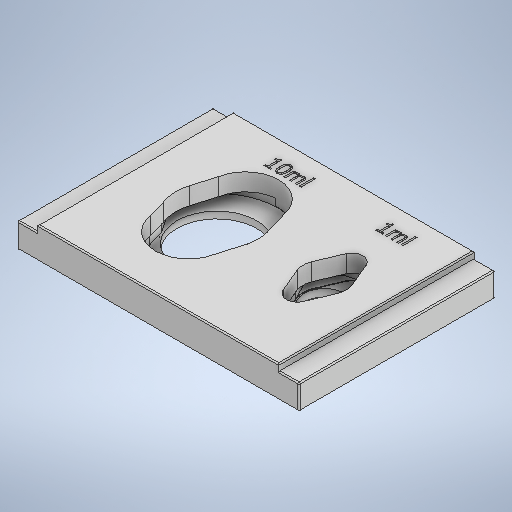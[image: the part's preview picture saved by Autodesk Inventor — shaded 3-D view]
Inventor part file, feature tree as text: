
AUTODESK INVENTOR PART (.ipt)
format: ipt  version: 2025 (Build 290162000, 162)  size: 602,624 bytes
history: native  units: mm
features: extrude x11, sketch x11, fillet x2, projected_geometry x1
ambient origin geometry x8: Origin, YZ Plane, XZ Plane, XY Plane, X Axis, Y Axis, Z Axis, Center Point
bodies: Volumenkörper1 (feature_tree)
feature tree (25):
  extrude  "Extrusion1"  Depth=50.0mm
  extrude  "Extrusion2"  Depth=20.4mm
  extrude  "Extrusion3"  Depth=10.0mm
  extrude  "Extrusion4"  Depth=2.0mm TaperAngle=0.0deg
  extrude  "Extrusion5"  Depth=1.57mm TaperAngle=0.0deg
  extrude  "Extrusion6"  Depth=0.48mm TaperAngle=0.0deg
  extrude  "Extrusion7"  TaperAngle=0.0deg  [1 undecoded]
  extrude  "Extrusion8"  TaperAngle=0.0deg  [1 undecoded]
  extrude  "Extrusion9"  Depth=4.47mm TaperAngle=0.0deg
  fillet  "Rundung1"  Radius=50.0mm
  fillet  "Rundung2"  [1 undecoded]
  extrude  "Extrusion10"  Depth=5.2mm
  extrude  "Extrusion11"  Depth=0.3mm
  sketch  "Skizze1"  dims[d0=72.0mm d1=50.0mm]
  sketch  "Skizze2"  dims[d2=2.0mm d3=0.0mm d4=20.4mm]
  sketch  "Skizze3"  dims[d5=10.4mm d6=10.0mm]
  sketch  "Skizze4"  dims[d7=17.5mm d8=2.0mm d9=0.0mm]
  sketch  "Skizze5"  dims[d10=1.57mm d11=0.0mm d20=1.57mm d21=0.0mm]
  sketch  "Skizze6"  dims[d41=1.85mm d42=0.0mm d43=0.48mm d44=0.0mm]
  sketch  "Skizze7"  dims[d45=2.3mm d46=0.0mm d47=0.0mm]
  sketch  "Skizze8"  dims[d48=0.0mm d49=0.0mm]
  sketch  "Skizze9"  dims[d50=0.0mm d51=4.47mm d52=0.0mm d53=50.0mm d54=0.0mm]
  projected_geometry  "Projizierte Kontur1"
  sketch  "Skizze10"  dims[d55=5.2mm d56=5.2mm]
  sketch  "Skizze11"  dims[d57=1.65mm d58=0.0mm d59=0.3mm d60=0.3mm d68=6.2mm d69=0.0mm d72=4.0mm d73=4.0mm d75=0.5mm d76=0.0mm d87=0.0mm d88=0.0mm]
note: 3 required parameter values undecoded (feature->parameter linkage not recoverable at this tier; creation-order binding heuristic only, values carry confidence <= 0.55)
